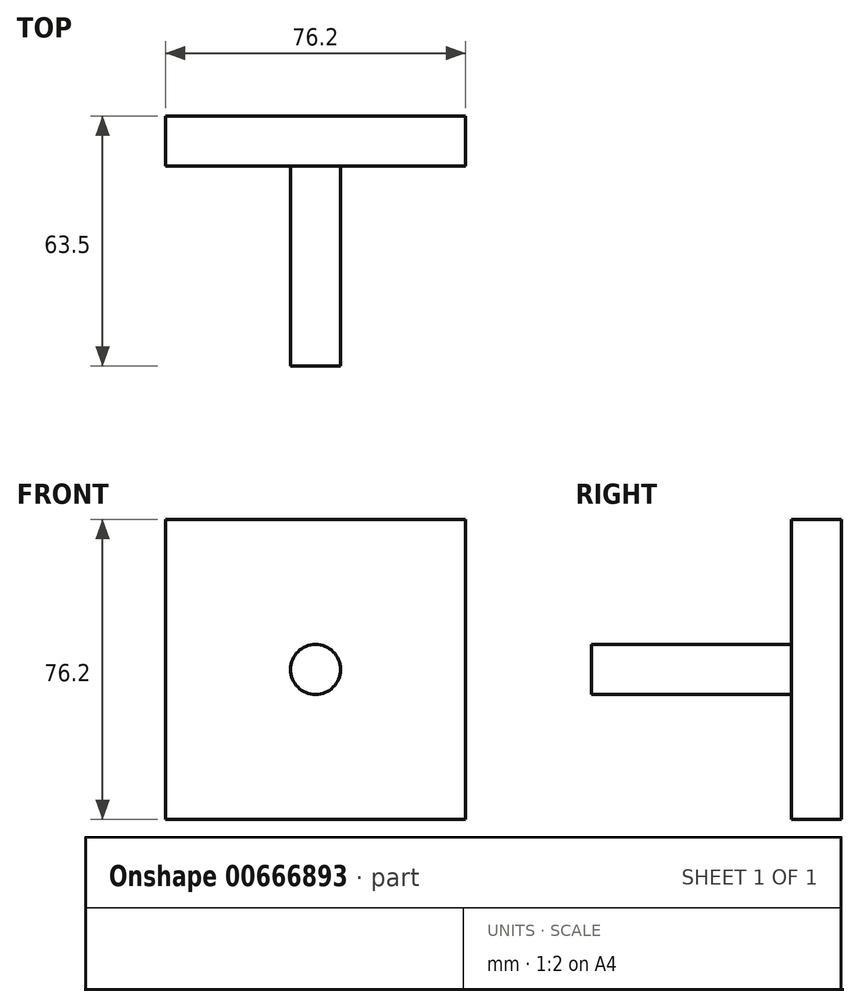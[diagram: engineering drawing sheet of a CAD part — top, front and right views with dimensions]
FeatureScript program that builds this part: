
annotation { "Feature Type Name" : "Feature", "Feature Type Description" : "" }
export const myFeature = defineFeature(function(context is Context, id is Id, definition is map)
    precondition{}
    {
        {
            var Q0;
            Q0=qCreatedBy(makeId("Front.planeOp"),FACE);
            var sketch = newSketch(context, id + "F0", { "sketchPlane" : qUnion([Q0])});
            skLineSegment(sketch, "E0.bottom", {"start": v(0, 0) * mm, "end": v(76.2, 0) * mm});
            skLineSegment(sketch, "E0.top", {"start": v(0, -76.2) * mm, "end": v(76.2, -76.2) * mm});
            skLineSegment(sketch, "E0.left", {"start": v(0, 0) * mm, "end": v(0, -76.2) * mm});
            skLineSegment(sketch, "E0.right", {"start": v(76.2, 0) * mm, "end": v(76.2, -76.2) * mm});
            skLineSegment(sketch, "E1", {"start": v(0, -38.1) * mm, "end": v(76.2, -38.1) * mm, "construction": true});
            skLineSegment(sketch, "E2", {"start": v(38.1, 0) * mm, "end": v(38.1, -76.2) * mm, "construction": true});
            skCircle(sketch, "E3", {"center": v(38.1, -38.1) * mm, "radius": 6.35 * mm});
            skSolve(sketch);
        }
        {
            var Q0;
            Q0=makeQuery(id+"F0.imprint","IMPRINT",FACE,{"disambiguationData":[TD([[makeQuery(id+"F0.imprint","IMPRINT",EDGE,{"derivedFrom":sQuery(id+"F0.wireOp",EDGE,"E0.bottom")}),-1.0]])]});
            extrude(context, id + "F1", {"entities" : qUnion([Q0]), "oppositeDirection" : true, "depth" : 12.7 * mm, "offsetDistance" : 25.4 * mm});
        }
        {
            var Q0;
            Q0=makeQuery(id+"F0.imprint","IMPRINT",FACE,{"disambiguationData":[TD([[makeQuery(id+"F0.imprint","IMPRINT",EDGE,{"derivedFrom":sQuery(id+"F0.wireOp",EDGE,"E3")}),1.0]])]});
            extrude(context, id + "F2", {"entities" : qUnion([Q0]), "operationType" : NewBodyOperationType.ADD, "depth" : 50.8 * mm, "offsetDistance" : 25.4 * mm, "hasSecondDirection" : true, "secondDirectionOppositeDirection" : true, "secondDirectionDepth" : 12.7 * mm});
        }
    });
